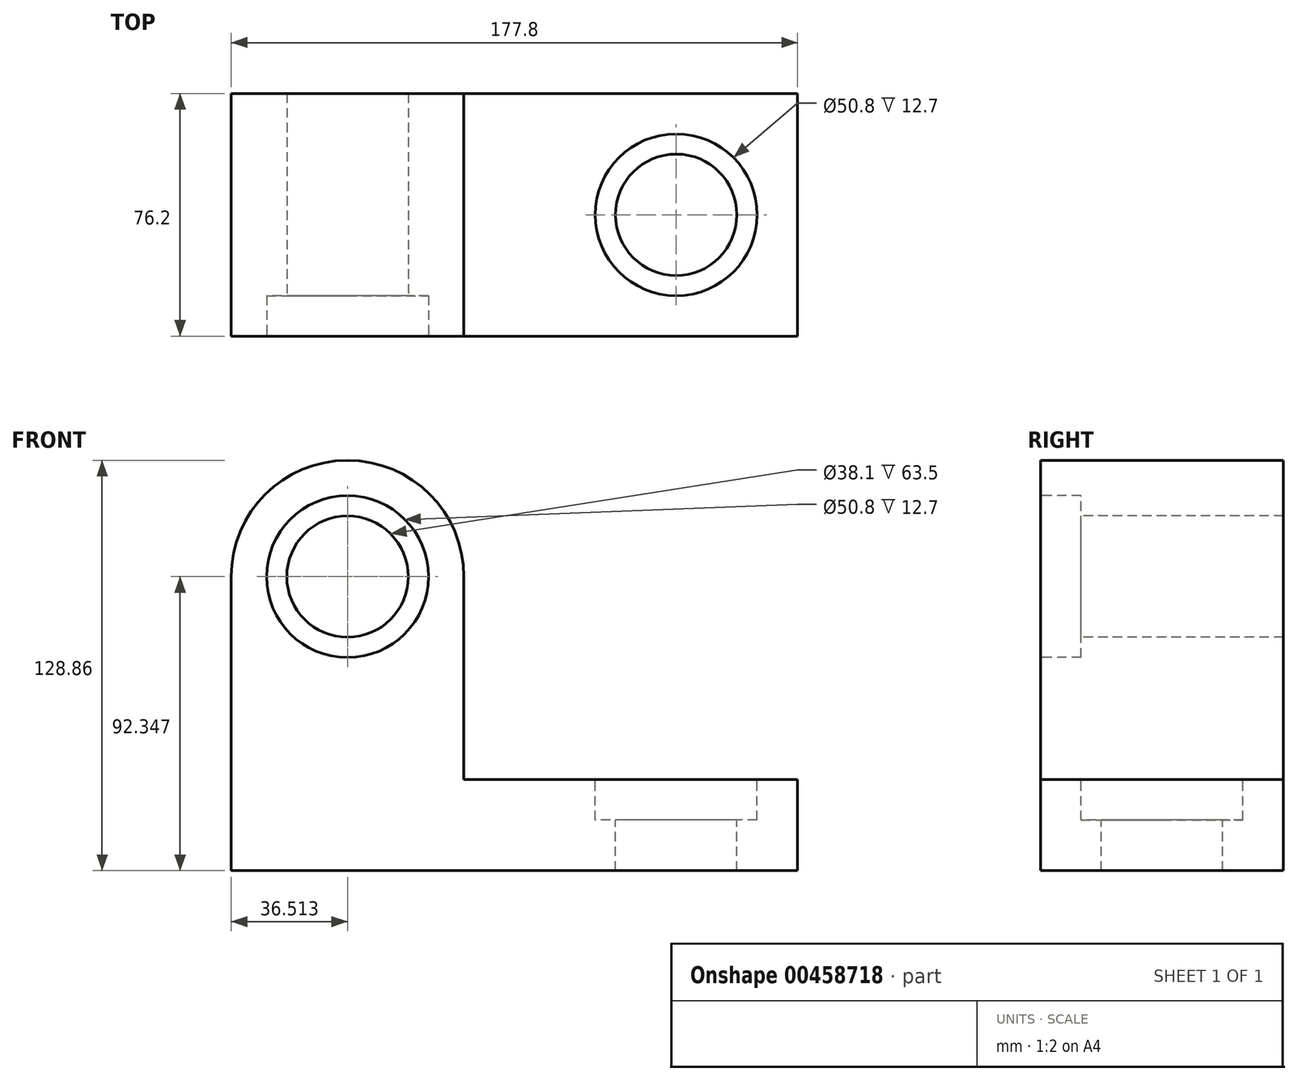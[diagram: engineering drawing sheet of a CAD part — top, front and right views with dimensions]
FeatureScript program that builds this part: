
annotation { "Feature Type Name" : "Feature", "Feature Type Description" : "" }
export const myFeature = defineFeature(function(context is Context, id is Id, definition is map)
    precondition{}
    {
        {
            var Q0;
            Q0=qCreatedBy(makeId("Top.planeOp"),FACE);
            var sketch = newSketch(context, id + "F0", { "sketchPlane" : qUnion([Q0])});
            skLineSegment(sketch, "E0.bottom", {"start": v(88.9, 38.1) * mm, "end": v(-88.9, 38.1) * mm});
            skLineSegment(sketch, "E0.top", {"start": v(88.9, -38.1) * mm, "end": v(-88.9, -38.1) * mm});
            skLineSegment(sketch, "E0.left", {"start": v(88.9, 38.1) * mm, "end": v(88.9, -38.1) * mm});
            skLineSegment(sketch, "E0.right", {"start": v(-88.9, 38.1) * mm, "end": v(-88.9, -38.1) * mm});
            skPoint(sketch, "E0.middle", {"position": v(0, 0) * mm});
            skLineSegment(sketch, "E1", {"start": v(-36.62, 38.1) * mm, "end": v(-36.62, -38.1) * mm});
            skPoint(sketch, "E2", {"position": v(46.32, 0) * mm});
            skSolve(sketch);
        }
        {
            var Q0;
            Q0=makeQuery(id+"F0.imprint","IMPRINT",FACE,{"disambiguationData":[TD([[makeQuery(id+"F0.imprint","IMPRINT",EDGE,{"derivedFrom":sQuery(id+"F0.wireOp",EDGE,"E0.bottom")}),1.0]])]});
            extrude(context, id + "F1", {"entities" : qUnion([Q0]), "depth" : 28.57 * mm});
        }
        {
            var Q0;
            Q0=makeQuery(id+"F1.opExtrude","CAP_FACE",FACE,{"disambiguationData":[OSD([sQuery(id+"F0.wireOp",EDGE,"E0.bottom"),sQuery(id+"F0.wireOp",EDGE,"E0.top"),sQuery(id+"F0.wireOp",EDGE,"E0.left"),sQuery(id+"F0.wireOp",EDGE,"E0.right")])],"isStart":false});
            var sketch = newSketch(context, id + "F2", { "sketchPlane" : qUnion([Q0])});
            skPoint(sketch, "E3", {"position": v(50.8, 0) * mm});
            skSolve(sketch);
        }
        {
            var Q0;
            Q0=sQuery(id+"F2.wireOp",VERTEX,"E3");
            var Q1;
            Q1=makeQuery(id+"F1.opExtrude","SWEPT_BODY",BODY,{"disambiguationData":[OSD([sQuery(id+"F0.wireOp",EDGE,"E0.bottom"),sQuery(id+"F0.wireOp",EDGE,"E0.top"),sQuery(id+"F0.wireOp",EDGE,"E0.left"),sQuery(id+"F0.wireOp",EDGE,"E0.right")])]});
            hole(context, id + "F3", {"style" : HoleStyle.C_BORE, "endStyle" : HoleEndStyle.THROUGH, "holeDiameter" : 38.1 * mm, "cBoreDiameter" : 50.8 * mm, "cBoreDepth" : 12.7 * mm, "isTappedThrough" : true, "tappedDepth" : 12.7 * mm, "tapClearance" : 3, "locations" : qUnion([Q0]), "scope" : qUnion([Q1])});
        }
        {
            var Q0;
            Q0=makeQuery(id+"F1.opExtrude","SWEPT_FACE",FACE,{"disambiguationData":[OSD([sQuery(id+"F0.wireOp",EDGE,"E0.top")])]});
            var sketch = newSketch(context, id + "F4", { "sketchPlane" : qUnion([Q0])});
            skLineSegment(sketch, "E4.bottom", {"start": v(-88.9, 0) * mm, "end": v(-15.88, 0) * mm});
            skLineSegment(sketch, "E4.top", {"start": v(-88.9, 92.35) * mm, "end": v(-15.88, 92.35) * mm});
            skLineSegment(sketch, "E4.left", {"start": v(-88.9, 0) * mm, "end": v(-88.9, 92.35) * mm});
            skLineSegment(sketch, "E4.right", {"start": v(-15.88, 0) * mm, "end": v(-15.88, 92.35) * mm});
            skArc(sketch, "E5", {"start": v(-15.88, 92.35) * mm, "mid": v(-52.39, 128.86) * mm, "end": v(-88.9, 92.35) * mm});
            skSolve(sketch);
        }
        {
            var Q0;
            {var subQ0=sQuery(id+"F4.wireOp",EDGE,"E4.top");Q0=makeQuery(id+"F4.imprint","IMPRINT",FACE,{"disambiguationData":[TD([[makeQuery(id+"F4.imprint","IMPRINT",EDGE,{"derivedFrom":subQ0}),-1.0]])]});}
            var Q1;
            Q1=makeQuery(id+"F4.imprint","IMPRINT",FACE,{"disambiguationData":[TD([[makeQuery(id+"F4.imprint","IMPRINT",EDGE,{"derivedFrom":sQuery(id+"F4.wireOp",EDGE,"E4.top")}),1.0]])]});
            extrude(context, id + "F5", {"entities" : qUnion([Q0, Q1]), "operationType" : NewBodyOperationType.ADD, "oppositeDirection" : true, "depth" : 76.2 * mm});
        }
        {
            var Q0;
            Q0=sQuery(id+"F4.wireOp",VERTEX,"E5.center");
            var Q1;
            Q1=makeQuery(id+"F1.opExtrude","SWEPT_BODY",BODY,{"disambiguationData":[OSD([sQuery(id+"F0.wireOp",EDGE,"E0.bottom"),sQuery(id+"F0.wireOp",EDGE,"E0.top"),sQuery(id+"F0.wireOp",EDGE,"E0.left"),sQuery(id+"F0.wireOp",EDGE,"E0.right")])]});
            hole(context, id + "F6", {"style" : HoleStyle.C_BORE, "endStyle" : HoleEndStyle.THROUGH, "holeDiameter" : 38.1 * mm, "cBoreDiameter" : 50.8 * mm, "cBoreDepth" : 12.7 * mm, "isTappedThrough" : true, "tappedDepth" : 12.7 * mm, "tapClearance" : 3, "locations" : qUnion([Q0]), "scope" : qUnion([Q1])});
        }
    });
